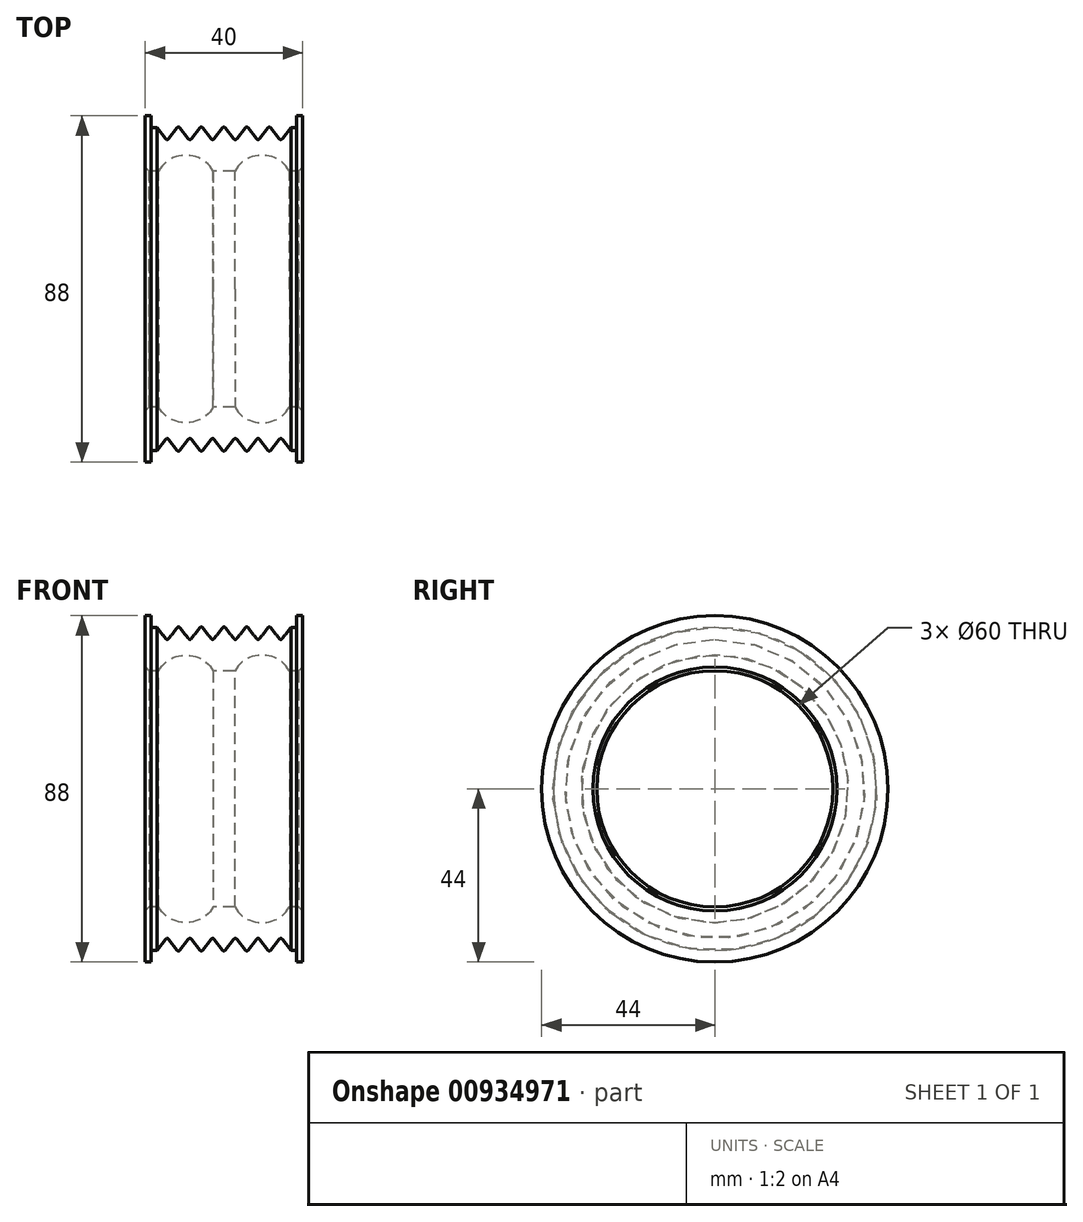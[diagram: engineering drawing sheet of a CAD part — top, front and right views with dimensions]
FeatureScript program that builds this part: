
annotation { "Feature Type Name" : "Feature", "Feature Type Description" : "" }
export const myFeature = defineFeature(function(context is Context, id is Id, definition is map)
    precondition{}
    {
        {
            var Q0;
            Q0=qCreatedBy(makeId("Front.planeOp"),FACE);
            var sketch = newSketch(context, id + "F0", { "sketchPlane" : qUnion([Q0])});
            skLineSegment(sketch, "E0", {"start": v(0, 30) * mm, "end": v(20, 30) * mm});
            skLineSegment(sketch, "E1", {"start": v(20, 30) * mm, "end": v(20, 44) * mm});
            skLineSegment(sketch, "E2", {"start": v(20, 44) * mm, "end": v(18.5, 44) * mm});
            skLineSegment(sketch, "E3", {"start": v(18.5, 44) * mm, "end": v(18.5, 41) * mm});
            skLineSegment(sketch, "E4", {"start": v(18.5, 41) * mm, "end": v(17, 41) * mm});
            skLineSegment(sketch, "E5", {"start": v(17, 41) * mm, "end": v(14.83, 38.2) * mm});
            skArc(sketch, "E6", {"start": v(14.83, 38.2) * mm, "mid": v(14.43, 38) * mm, "end": v(14.03, 38.2) * mm});
            skLineSegment(sketch, "E7", {"start": v(14.03, 38.2) * mm, "end": v(11.86, 41) * mm});
            skArc(sketch, "E8", {"start": v(11.86, 41) * mm, "mid": v(11.54, 41.15) * mm, "end": v(11.23, 41) * mm});
            skLineSegment(sketch, "E9", {"start": v(11.23, 41) * mm, "end": v(9.05, 38.2) * mm});
            skArc(sketch, "E10", {"start": v(9.05, 38.2) * mm, "mid": v(8.66, 38) * mm, "end": v(8.26, 38.2) * mm});
            skLineSegment(sketch, "E11", {"start": v(8.26, 38.2) * mm, "end": v(6.09, 41) * mm});
            skArc(sketch, "E12", {"start": v(6.09, 41) * mm, "mid": v(5.77, 41.15) * mm, "end": v(5.46, 41) * mm});
            skLineSegment(sketch, "E13", {"start": v(5.46, 41) * mm, "end": v(3.28, 38.2) * mm});
            skArc(sketch, "E14", {"start": v(3.28, 38.2) * mm, "mid": v(2.89, 38) * mm, "end": v(2.5, 38.2) * mm});
            skLineSegment(sketch, "E15", {"start": v(2.5, 38.2) * mm, "end": v(0.32, 41) * mm});
            skArc(sketch, "E16", {"start": v(0.32, 41) * mm, "mid": v(0.18, 41.11) * mm, "end": v(0, 41.15) * mm});
            skCircle(sketch, "E17", {"center": v(14.43, 43.5) * mm, "radius": 0.86 * mm, "construction": true});
            skArc(sketch, "E18.MirrorCS", {"start": v(-9.05, 38.2) * mm, "mid": v(-8.66, 38) * mm, "end": v(-8.26, 38.2) * mm});
            skArc(sketch, "E19.MirrorCS", {"start": v(-3.28, 38.2) * mm, "mid": v(-2.89, 38) * mm, "end": v(-2.5, 38.2) * mm});
            skArc(sketch, "E20.MirrorCS", {"start": v(-11.86, 41) * mm, "mid": v(-11.54, 41.15) * mm, "end": v(-11.23, 41) * mm});
            skLineSegment(sketch, "E21.MirrorCS", {"start": v(-18.5, 41) * mm, "end": v(-17, 41) * mm});
            skArc(sketch, "E22.MirrorCS", {"start": v(-0.32, 41) * mm, "mid": v(-0.18, 41.11) * mm, "end": v(0, 41.15) * mm});
            skArc(sketch, "E23.MirrorCS", {"start": v(-14.83, 38.2) * mm, "mid": v(-14.43, 38) * mm, "end": v(-14.03, 38.2) * mm});
            skArc(sketch, "E24.MirrorCS", {"start": v(-6.09, 41) * mm, "mid": v(-5.77, 41.15) * mm, "end": v(-5.46, 41) * mm});
            skLineSegment(sketch, "E25.MirrorCS", {"start": v(-20, 44) * mm, "end": v(-18.5, 44) * mm});
            skLineSegment(sketch, "E26.MirrorCS", {"start": v(-18.5, 44) * mm, "end": v(-18.5, 41) * mm});
            skLineSegment(sketch, "E27.MirrorCS", {"start": v(-11.23, 41) * mm, "end": v(-9.05, 38.2) * mm});
            skLineSegment(sketch, "E28.MirrorCS", {"start": v(-2.5, 38.2) * mm, "end": v(-0.32, 41) * mm});
            skLineSegment(sketch, "E29.MirrorCS", {"start": v(-5.46, 41) * mm, "end": v(-3.28, 38.2) * mm});
            skLineSegment(sketch, "E30.MirrorCS", {"start": v(-8.26, 38.2) * mm, "end": v(-6.09, 41) * mm});
            skLineSegment(sketch, "E31.MirrorCS", {"start": v(-17, 41) * mm, "end": v(-14.83, 38.2) * mm});
            skLineSegment(sketch, "E32.MirrorCS", {"start": v(-14.03, 38.2) * mm, "end": v(-11.86, 41) * mm});
            skCircle(sketch, "E33.MirrorC", {"center": v(-14.43, 43.5) * mm, "radius": 0.86 * mm, "construction": true});
            skLineSegment(sketch, "E34.MirrorCS", {"start": v(0, 30) * mm, "end": v(-20, 30) * mm});
            skLineSegment(sketch, "E35.MirrorCS", {"start": v(-20, 30) * mm, "end": v(-20, 44) * mm});
            skLineSegment(sketch, "E36", {"start": v(-40, 0) * mm, "end": v(40, 0) * mm, "construction": true});
            skSolve(sketch);
        }
        {
            var Q0;
            Q0=makeQuery(id+"F0.imprint","IMPRINT",FACE,{"disambiguationData":[TD([[makeQuery(id+"F0.imprint","IMPRINT",EDGE,{"derivedFrom":sQuery(id+"F0.wireOp",EDGE,"E0")}),1.0]])]});
            var Q1;
            Q1=sQuery(id+"F0.wireOp",EDGE,"E36");
            var Q2;
            Q2=sQuery(id+"F0.wireOp",EDGE,"E36");
            revolve(context, id + "F1", {"surfaceOperationType" : NewSurfaceOperationType.NEW, "entities" : qUnion([Q0]), "surfaceEntities" : qUnion([Q1]), "axis" : qUnion([Q2]), "revolveType" : RevolveType.FULL});
        }
        {
            var Q0;
            Q0=qCreatedBy(makeId("Front.planeOp"),FACE);
            var sketch = newSketch(context, id + "F2", { "sketchPlane" : qUnion([Q0])});
            skCircle(sketch, "E37", {"center": v(-9.68, 26) * mm, "radius": 8 * mm});
            skCircle(sketch, "E38.MirrorC", {"center": v(9.68, 26) * mm, "radius": 8 * mm});
            skSolve(sketch);
        }
        {
            var Q0;
            Q0 = qSketchRegion(id + "F2", true);
            var Q1;
            Q1=sQuery(id+"F0.wireOp",EDGE,"E36");
            revolve(context, id + "F3", {"operationType" : NewBodyOperationType.REMOVE, "surfaceOperationType" : NewSurfaceOperationType.NEW, "entities" : qUnion([Q0]), "axis" : qUnion([Q1]), "revolveType" : RevolveType.FULL, "oppositeDirection" : true});
        }
        {
            var Q0;
            Q0=makeQuery(id+"F1.opRevolve","SWEPT_EDGE",EDGE,{"disambiguationData":[OSD([sQuery(id+"F0.wireOp",EDGE,"E0"),sQuery(id+"F0.wireOp",EDGE,"E1")])]});
            var Q1;
            Q1=makeQuery(id+"F1.opRevolve","SWEPT_EDGE",EDGE,{"disambiguationData":[OSD([sQuery(id+"F0.wireOp",EDGE,"E34.MirrorCS"),sQuery(id+"F0.wireOp",EDGE,"E35.MirrorCS")])]});
            chamfer(context, id + "F4", {"entities" : qUnion([Q0, Q1]), "width" : 1 * mm, "tangentPropagation" : true});
        }
    });
